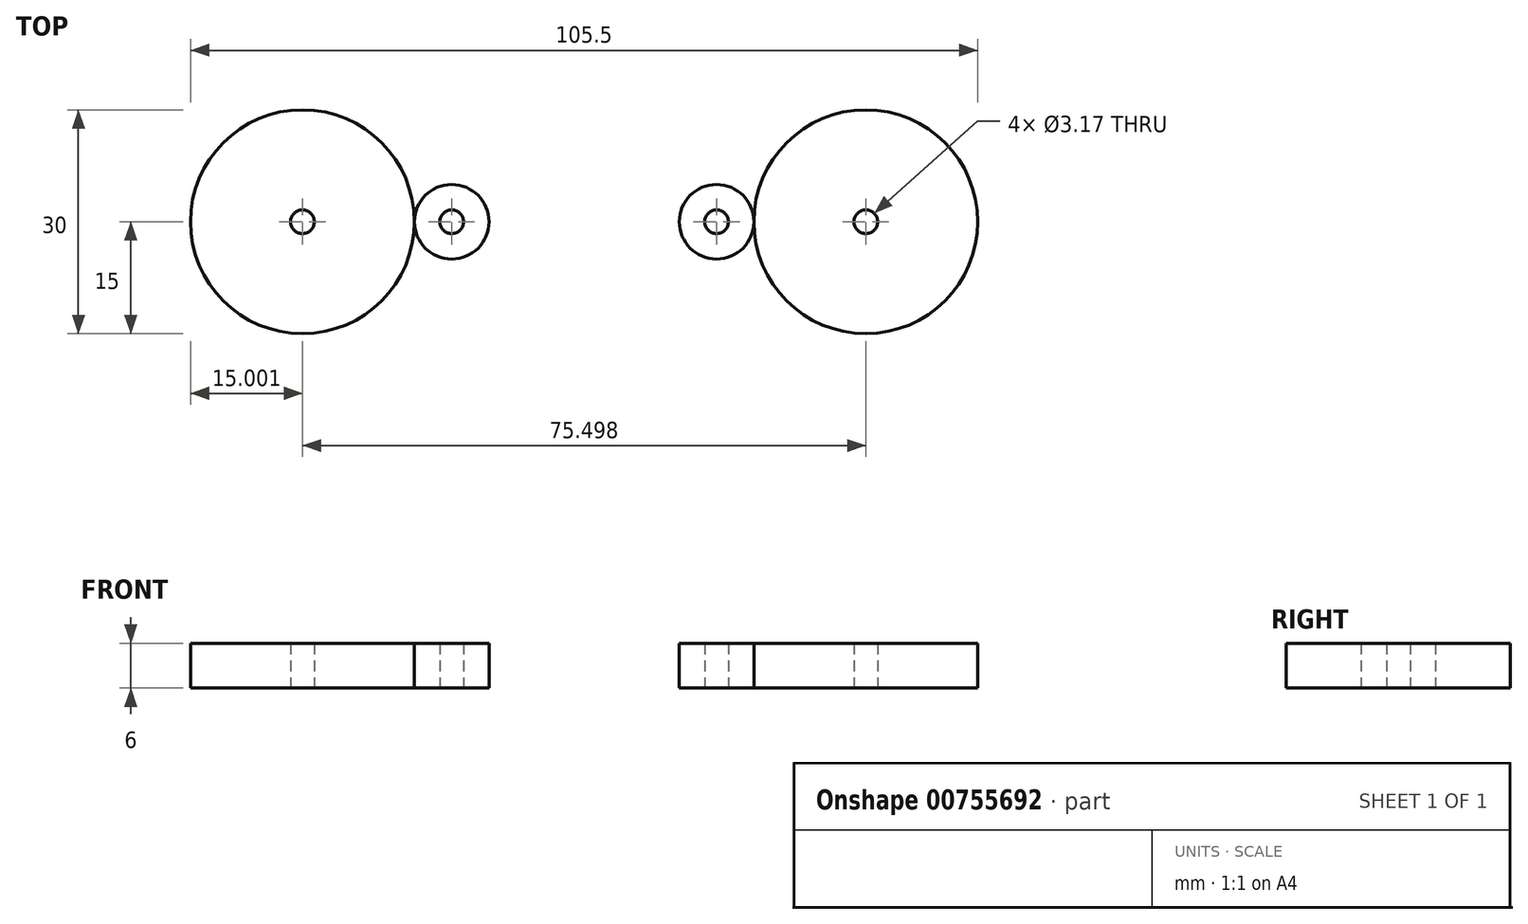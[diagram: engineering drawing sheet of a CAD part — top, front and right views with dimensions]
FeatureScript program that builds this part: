
annotation { "Feature Type Name" : "Feature", "Feature Type Description" : "" }
export const myFeature = defineFeature(function(context is Context, id is Id, definition is map)
    precondition{}
    {
        {
            var Q0;
            Q0=qCreatedBy(makeId("Top.planeOp"),FACE);
            var sketch = newSketch(context, id + "F0", { "sketchPlane" : qUnion([Q0])});
            skCircle(sketch, "E0", {"center": v(-17.75, 0) * mm, "radius": 5 * mm});
            skCircle(sketch, "E1", {"center": v(-37.75, 0) * mm, "radius": 15 * mm});
            skCircle(sketch, "E2", {"center": v(-37.75, 0) * mm, "radius": 1.59 * mm});
            skCircle(sketch, "E3", {"center": v(-17.75, 0) * mm, "radius": 1.59 * mm});
            skLineSegment(sketch, "E4", {"start": v(0, 76.55) * mm, "end": v(0, -75.65) * mm});
            skCircle(sketch, "E5.MirrorC", {"center": v(37.75, 0) * mm, "radius": 15 * mm});
            skCircle(sketch, "E6.MirrorC", {"center": v(17.75, 0) * mm, "radius": 5 * mm});
            skCircle(sketch, "E7", {"center": v(37.75, 0) * mm, "radius": 1.59 * mm});
            skCircle(sketch, "E8", {"center": v(17.75, 0) * mm, "radius": 1.59 * mm});
            skSolve(sketch);
        }
        {
            var Q0;
            Q0 = qSketchRegion(id + "F0", true);
            extrude(context, id + "F1", {"entities" : qUnion([Q0]), "depth" : 6 * mm, "offsetDistance" : 25.4 * mm});
        }
    });
